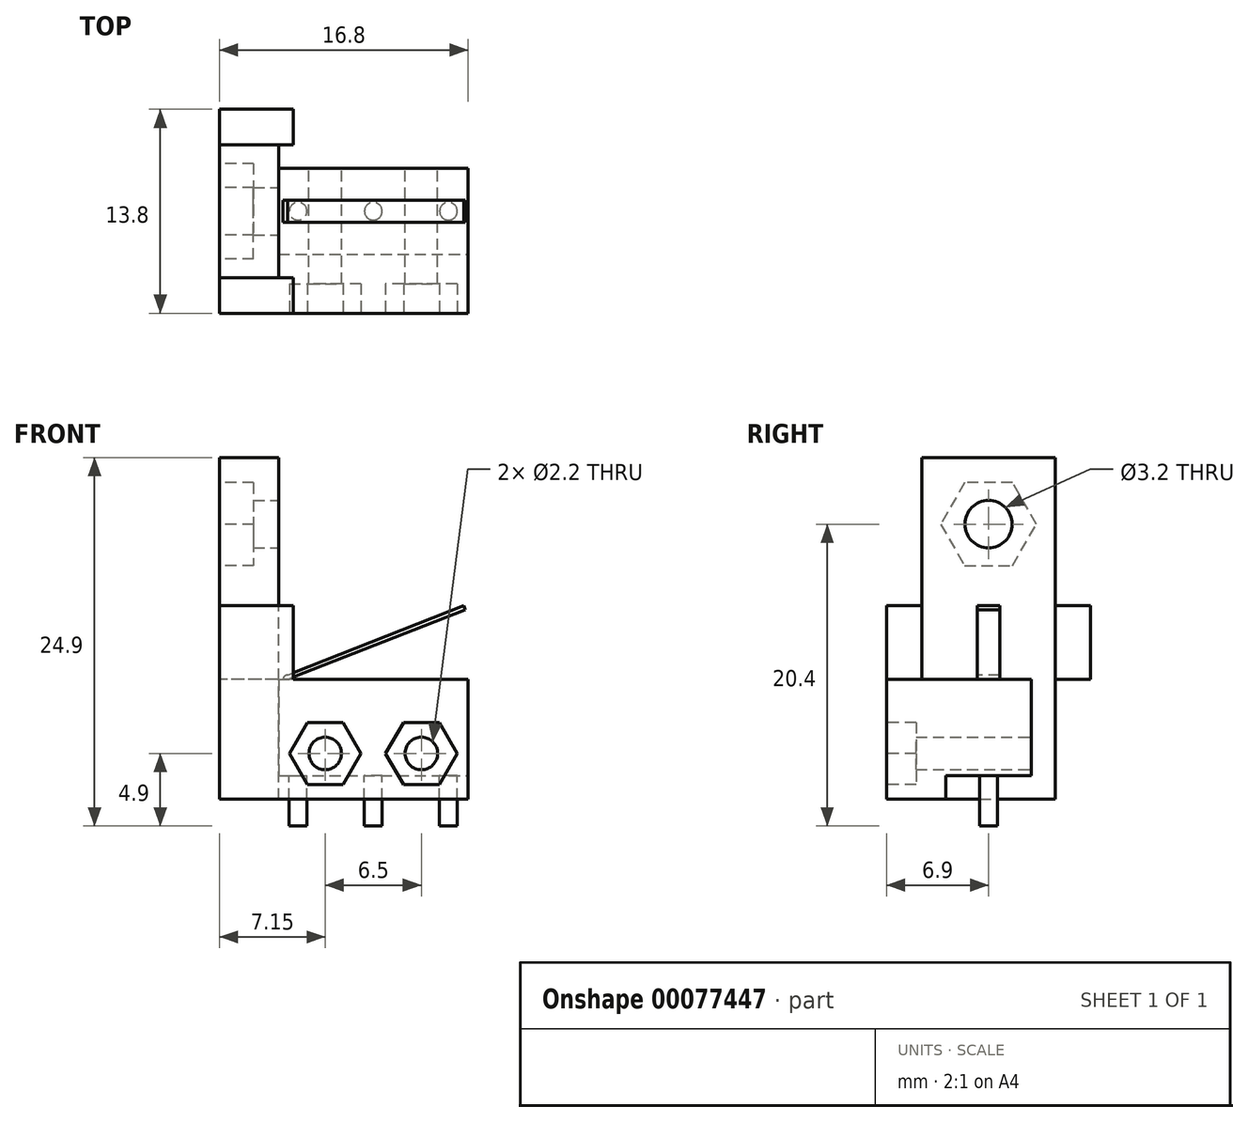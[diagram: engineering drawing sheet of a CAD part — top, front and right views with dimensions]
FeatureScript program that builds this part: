
annotation { "Feature Type Name" : "Feature", "Feature Type Description" : "" }
export const myFeature = defineFeature(function(context is Context, id is Id, definition is map)
    precondition{}
    {
        {
            var Q0;
            Q0=qCreatedBy(makeId("Front.planeOp"),FACE);
            var sketch = newSketch(context, id + "F0", { "sketchPlane" : qUnion([Q0])});
            skLineSegment(sketch, "E0.bottom", {"start": v(-6.4, 6.5) * mm, "end": v(6.4, 6.5) * mm});
            skLineSegment(sketch, "E0.top", {"start": v(-6.4, 0) * mm, "end": v(6.4, 0) * mm});
            skLineSegment(sketch, "E0.left", {"start": v(-6.4, 6.5) * mm, "end": v(-6.4, 0) * mm});
            skLineSegment(sketch, "E0.right", {"start": v(6.4, 6.5) * mm, "end": v(6.4, 0) * mm});
            skCircle(sketch, "E1", {"center": v(3.25, 1.5) * mm, "radius": 1.1 * mm});
            skCircle(sketch, "E2", {"center": v(-3.25, 1.5) * mm, "radius": 1.1 * mm});
            skLineSegment(sketch, "E3", {"start": v(0, 0.48) * mm, "end": v(0, 13.87) * mm, "construction": true});
            skSolve(sketch);
        }
        {
            var Q0;
            Q0=qSketchRegion(id+"F0",true);
            extrude(context, id + "F1", {"entities" : qUnion([Q0]), "depth" : 5.8 * mm});
        }
        {
            var Q0;
            Q0=makeQuery(id+"F1.opExtrude","SWEPT_FACE",FACE,{"disambiguationData":[OSD([sQuery(id+"F0.wireOp",EDGE,"E0.top")])]});
            var sketch = newSketch(context, id + "F2", { "sketchPlane" : qUnion([Q0])});
            skLineSegment(sketch, "E4", {"start": v(0, 12.32) * mm, "end": v(0, -7.08) * mm, "construction": true});
            skCircle(sketch, "E5", {"center": v(-5.08, 2.9) * mm, "radius": 0.6 * mm});
            skCircle(sketch, "E6", {"center": v(0, 2.9) * mm, "radius": 0.6 * mm});
            skCircle(sketch, "E7", {"center": v(5.08, 2.9) * mm, "radius": 0.6 * mm});
            skLineSegment(sketch, "E8", {"start": v(-20.59, 2.9) * mm, "end": v(16.53, 2.9) * mm, "construction": true});
            skPoint(sketch, "E9", {"position": v(-6.4, 2.9) * mm});
            skSolve(sketch);
        }
        {
            var Q0;
            Q0=qSketchRegion(id+"F2",true);
            extrude(context, id + "F3", {"entities" : qUnion([Q0]), "operationType" : NewBodyOperationType.ADD, "depth" : 3.4 * mm});
        }
        {
            var Q0;
            Q0=makeQuery(id+"F1.opExtrude","CAP_FACE",FACE,{"disambiguationData":[OSD([sQuery(id+"F0.wireOp",EDGE,"E0.bottom"),sQuery(id+"F0.wireOp",EDGE,"E0.top"),sQuery(id+"F0.wireOp",EDGE,"E0.left"),sQuery(id+"F0.wireOp",EDGE,"E0.right"),sQuery(id+"F0.wireOp",EDGE,"E1"),sQuery(id+"F0.wireOp",EDGE,"E2")])],"isStart":true});
            var Q1;
            Q1=makeQuery(id+"F1.opExtrude","CAP_FACE",FACE,{"disambiguationData":[OSD([sQuery(id+"F0.wireOp",EDGE,"E0.bottom"),sQuery(id+"F0.wireOp",EDGE,"E0.top"),sQuery(id+"F0.wireOp",EDGE,"E0.left"),sQuery(id+"F0.wireOp",EDGE,"E0.right"),sQuery(id+"F0.wireOp",EDGE,"E1"),sQuery(id+"F0.wireOp",EDGE,"E2")])],"isStart":false});
            cPlane(context, id + "F4", {"entities" : qUnion([Q0, Q1]), "cplaneType" : CPlaneType.MID_PLANE, "offset" : 150 * mm, "width" : 150 * mm, "height" : 150 * mm});
        }
        {
            var Q0;
            Q0=qCreatedBy(id+"F4.planeOp",FACE);
            var sketch = newSketch(context, id + "F5", { "sketchPlane" : qUnion([Q0])});
            skLineSegment(sketch, "E10", {"start": v(16.26, 6.5) * mm, "end": v(-15.15, 6.5) * mm, "construction": true});
            skLineSegment(sketch, "E11", {"start": v(5.8, 6.5) * mm, "end": v(-6.22, 11.22) * mm});
            skLineSegment(sketch, "E12", {"start": v(5.8, 6.8) * mm, "end": v(-6.1, 11.5) * mm});
            skLineSegment(sketch, "E13", {"start": v(-6.1, 11.5) * mm, "end": v(-6.22, 11.22) * mm});
            skLineSegment(sketch, "E14", {"start": v(5.8, 6.5) * mm, "end": v(6.1, 6.5) * mm});
            skArc(sketch, "E15", {"start": v(6.1, 6.5) * mm, "mid": v(6.01, 6.71) * mm, "end": v(5.8, 6.8) * mm});
            skLineSegment(sketch, "E16", {"start": v(5.8, 6.5) * mm, "end": v(5.8, 6.8) * mm, "construction": true});
            skLineSegment(sketch, "E17", {"start": v(15.7, 1.5) * mm, "end": v(-17.73, 1.5) * mm, "construction": true});
            skPoint(sketch, "E18", {"position": v(-3.25, 1.5) * mm});
            skPoint(sketch, "E19", {"position": v(3.25, 1.5) * mm});
            skSolve(sketch);
        }
        {
            var Q0;
            Q0=qSketchRegion(id+"F5",true);
            extrude(context, id + "F6", {"entities" : qUnion([Q0]), "operationType" : NewBodyOperationType.ADD, "endBound" : BoundingType.SYMMETRIC, "depth" : 1.5 * mm});
        }
        {
            var Q0;
            Q0=makeQuery(id+"F1.opExtrude","CAP_FACE",FACE,{"disambiguationData":[OSD([sQuery(id+"F0.wireOp",EDGE,"E0.bottom"),sQuery(id+"F0.wireOp",EDGE,"E0.top"),sQuery(id+"F0.wireOp",EDGE,"E0.left"),sQuery(id+"F0.wireOp",EDGE,"E0.right"),sQuery(id+"F0.wireOp",EDGE,"E1"),sQuery(id+"F0.wireOp",EDGE,"E2")])],"isStart":false});
            var sketch = newSketch(context, id + "F7", { "sketchPlane" : qUnion([Q0])});
            skLineSegment(sketch, "E20.bottom", {"start": v(6.4, -1.6) * mm, "end": v(-6.4, -1.6) * mm});
            skLineSegment(sketch, "E20.top", {"start": v(6.4, 6.5) * mm, "end": v(-6.4, 6.5) * mm});
            skLineSegment(sketch, "E20.left", {"start": v(6.4, -1.6) * mm, "end": v(6.4, 6.5) * mm});
            skLineSegment(sketch, "E20.right", {"start": v(-6.4, -1.6) * mm, "end": v(-6.4, 6.5) * mm});
            skLineSegment(sketch, "E21", {"start": v(0, -13.07) * mm, "end": v(0, 21.12) * mm, "construction": true});
            skPoint(sketch, "E22", {"position": v(3.25, 1.5) * mm});
            skPoint(sketch, "E23", {"position": v(-3.25, 1.5) * mm});
            skLineSegment(sketch, "E24", {"start": v(3.25, 1.5) * mm, "end": v(-3.25, 1.5) * mm, "construction": true});
            skCircle(sketch, "E25", {"center": v(3.25, 1.5) * mm, "radius": 1.1 * mm});
            skCircle(sketch, "E26", {"center": v(-3.25, 1.5) * mm, "radius": 1.1 * mm});
            skSolve(sketch);
        }
        {
            var Q0;
            Q0=qSketchRegion(id+"F7",true);
            extrude(context, id + "F8", {"entities" : qUnion([Q0]), "depth" : 4 * mm});
        }
        {
            var Q0;
            Q0=makeQuery(id+"F8.opExtrude","CAP_FACE",FACE,{"disambiguationData":[OSD([sQuery(id+"F7.wireOp",EDGE,"E20.bottom"),sQuery(id+"F7.wireOp",EDGE,"E20.top"),sQuery(id+"F7.wireOp",EDGE,"E20.left"),sQuery(id+"F7.wireOp",EDGE,"E20.right")])],"isStart":false});
            var sketch = newSketch(context, id + "F9", { "sketchPlane" : qUnion([Q0])});
            skLineSegment(sketch, "E27", {"start": v(-3.25, -7.44) * mm, "end": v(-3.25, 10.28) * mm, "construction": true});
            skCircle(sketch, "E28.cCircle", {"center": v(-3.25, 1.5) * mm, "radius": 2.1 * mm, "construction": true});
            skLineSegment(sketch, "E28.0", {"start": v(-2.04, -0.6) * mm, "end": v(-4.46, -0.6) * mm});
            skLineSegment(sketch, "E28.1", {"start": v(-4.46, -0.6) * mm, "end": v(-5.67, 1.5) * mm});
            skLineSegment(sketch, "E28.2", {"start": v(-5.67, 1.5) * mm, "end": v(-4.46, 3.6) * mm});
            skLineSegment(sketch, "E28.3", {"start": v(-4.46, 3.6) * mm, "end": v(-2.04, 3.6) * mm});
            skLineSegment(sketch, "E28.4", {"start": v(-2.04, 3.6) * mm, "end": v(-0.83, 1.5) * mm});
            skLineSegment(sketch, "E28.5", {"start": v(-0.83, 1.5) * mm, "end": v(-2.04, -0.6) * mm});
            skPoint(sketch, "E28.0.midPoint", {"position": v(-3.25, -0.6) * mm});
            skLineSegment(sketch, "E29", {"start": v(0, -5.2) * mm, "end": v(0, 11) * mm, "construction": true});
            skLineSegment(sketch, "E30.MirrorCS", {"start": v(0.83, 1.5) * mm, "end": v(2.04, -0.6) * mm});
            skPoint(sketch, "E31.MirrorP", {"position": v(3.25, -0.6) * mm});
            skLineSegment(sketch, "E32.MirrorCS", {"start": v(5.67, 1.5) * mm, "end": v(4.46, 3.6) * mm});
            skLineSegment(sketch, "E33.MirrorCS", {"start": v(4.46, 3.6) * mm, "end": v(2.04, 3.6) * mm});
            skLineSegment(sketch, "E34.MirrorCS", {"start": v(2.04, 3.6) * mm, "end": v(0.83, 1.5) * mm});
            skCircle(sketch, "E35.MirrorC", {"center": v(3.25, 1.5) * mm, "radius": 2.1 * mm, "construction": true});
            skLineSegment(sketch, "E36.MirrorCS", {"start": v(4.46, -0.6) * mm, "end": v(5.67, 1.5) * mm});
            skLineSegment(sketch, "E37.MirrorCS", {"start": v(2.04, -0.6) * mm, "end": v(4.46, -0.6) * mm});
            skSolve(sketch);
        }
        {
            var Q0;
            Q0=qSketchRegion(id+"F9",true);
            extrude(context, id + "F10", {"entities" : qUnion([Q0]), "operationType" : NewBodyOperationType.REMOVE, "oppositeDirection" : true, "depth" : 2 * mm});
        }
        {
            var Q0;
            Q0=makeQuery(id+"F1.opExtrude","SWEPT_FACE",FACE,{"disambiguationData":[OSD([sQuery(id+"F0.wireOp",EDGE,"E0.left")])]});
            var sketch = newSketch(context, id + "F11", { "sketchPlane" : qUnion([Q0])});
            skLineSegment(sketch, "E38.top", {"start": v(7.4, 21.5) * mm, "end": v(-1.6, 21.5) * mm});
            skLineSegment(sketch, "E38.left", {"start": v(7.4, 6.5) * mm, "end": v(7.4, 21.5) * mm});
            skLineSegment(sketch, "E38.right", {"start": v(-1.6, -1.6) * mm, "end": v(-1.6, 21.5) * mm});
            skLineSegment(sketch, "E39", {"start": v(2.9, 5.34) * mm, "end": v(2.9, 57.94) * mm, "construction": true});
            skLineSegment(sketch, "E40", {"start": v(7.4, 6.5) * mm, "end": v(9.8, 6.5) * mm});
            skLineSegment(sketch, "E41", {"start": v(9.8, 6.5) * mm, "end": v(9.8, -1.6) * mm});
            skLineSegment(sketch, "E42", {"start": v(9.8, -1.6) * mm, "end": v(-1.6, -1.6) * mm});
            skPoint(sketch, "E43", {"position": v(2.9, 21.5) * mm});
            skLineSegment(sketch, "E44", {"start": v(18.07, 9.5) * mm, "end": v(-14.2, 9.5) * mm, "construction": true});
            skCircle(sketch, "E45", {"center": v(2.9, 17) * mm, "radius": 1.6 * mm});
            skSolve(sketch);
        }
        {
            var Q0;
            Q0=qSketchRegion(id+"F11",true);
            extrude(context, id + "F12", {"entities" : qUnion([Q0]), "operationType" : NewBodyOperationType.ADD, "depth" : 4 * mm});
        }
        {
            var Q0;
            Q0=makeQuery(id+"F12.opExtrude","CAP_FACE",FACE,{"disambiguationData":[OSD([sQuery(id+"F11.wireOp",EDGE,"E38.top"),sQuery(id+"F11.wireOp",EDGE,"E38.left"),sQuery(id+"F11.wireOp",EDGE,"E38.right"),sQuery(id+"F11.wireOp",EDGE,"E40"),sQuery(id+"F11.wireOp",EDGE,"E41"),sQuery(id+"F11.wireOp",EDGE,"E42"),sQuery(id+"F11.wireOp",EDGE,"E45")])],"isStart":false});
            var sketch = newSketch(context, id + "F13", { "sketchPlane" : qUnion([Q0])});
            skLineSegment(sketch, "E46", {"start": v(2.9, 27.74) * mm, "end": v(2.9, 6.94) * mm, "construction": true});
            skPoint(sketch, "E47", {"position": v(2.9, 17) * mm});
            skCircle(sketch, "E48.cCircle", {"center": v(2.9, 17) * mm, "radius": 2.8 * mm, "construction": true});
            skLineSegment(sketch, "E48.0", {"start": v(4.52, 14.2) * mm, "end": v(1.28, 14.2) * mm});
            skLineSegment(sketch, "E48.1", {"start": v(1.28, 14.2) * mm, "end": v(-0.33, 17) * mm});
            skLineSegment(sketch, "E48.2", {"start": v(-0.33, 17) * mm, "end": v(1.28, 19.8) * mm});
            skLineSegment(sketch, "E48.3", {"start": v(1.28, 19.8) * mm, "end": v(4.52, 19.8) * mm});
            skLineSegment(sketch, "E48.4", {"start": v(4.52, 19.8) * mm, "end": v(6.13, 17) * mm});
            skLineSegment(sketch, "E48.5", {"start": v(6.13, 17) * mm, "end": v(4.52, 14.2) * mm});
            skPoint(sketch, "E48.0.midPoint", {"position": v(2.9, 14.2) * mm});
            skSolve(sketch);
        }
        {
            var Q0;
            Q0=qSketchRegion(id+"F13",true);
            extrude(context, id + "F14", {"entities" : qUnion([Q0]), "operationType" : NewBodyOperationType.REMOVE, "oppositeDirection" : true, "depth" : 2.3 * mm});
        }
        {
            var Q0;
            Q0=makeQuery(id+"F12.opExtrude","CAP_FACE",FACE,{"disambiguationData":[OSD([sQuery(id+"F11.wireOp",EDGE,"E38.top"),sQuery(id+"F11.wireOp",EDGE,"E38.left"),sQuery(id+"F11.wireOp",EDGE,"E38.right"),sQuery(id+"F11.wireOp",EDGE,"E40"),sQuery(id+"F11.wireOp",EDGE,"E41"),sQuery(id+"F11.wireOp",EDGE,"E42"),sQuery(id+"F11.wireOp",EDGE,"E45")])],"isStart":false});
            var sketch = newSketch(context, id + "F15", { "sketchPlane" : qUnion([Q0])});
            skLineSegment(sketch, "E49", {"start": v(2.9, -3.9) * mm, "end": v(2.9, 26.18) * mm, "construction": true});
            skLineSegment(sketch, "E50.bottom", {"start": v(9.8, 6.5) * mm, "end": v(7.4, 6.5) * mm});
            skLineSegment(sketch, "E50.top", {"start": v(9.8, 11.5) * mm, "end": v(7.4, 11.5) * mm});
            skLineSegment(sketch, "E50.left", {"start": v(9.8, 6.5) * mm, "end": v(9.8, 11.5) * mm});
            skLineSegment(sketch, "E50.right", {"start": v(7.4, 6.5) * mm, "end": v(7.4, 11.5) * mm});
            skLineSegment(sketch, "E51.MirrorCS", {"start": v(-1.6, 6.5) * mm, "end": v(-1.6, 11.5) * mm});
            skLineSegment(sketch, "E52.MirrorCS", {"start": v(-4, 6.5) * mm, "end": v(-1.6, 6.5) * mm});
            skLineSegment(sketch, "E53.MirrorCS", {"start": v(-4, 11.5) * mm, "end": v(-1.6, 11.5) * mm});
            skLineSegment(sketch, "E54.MirrorCS", {"start": v(-4, 6.5) * mm, "end": v(-4, 11.5) * mm});
            skSolve(sketch);
        }
        {
            var Q0;
            Q0=qSketchRegion(id+"F15",true);
            extrude(context, id + "F16", {"entities" : qUnion([Q0]), "operationType" : NewBodyOperationType.ADD, "oppositeDirection" : true, "depth" : (4 + 1) * mm});
        }
    });
